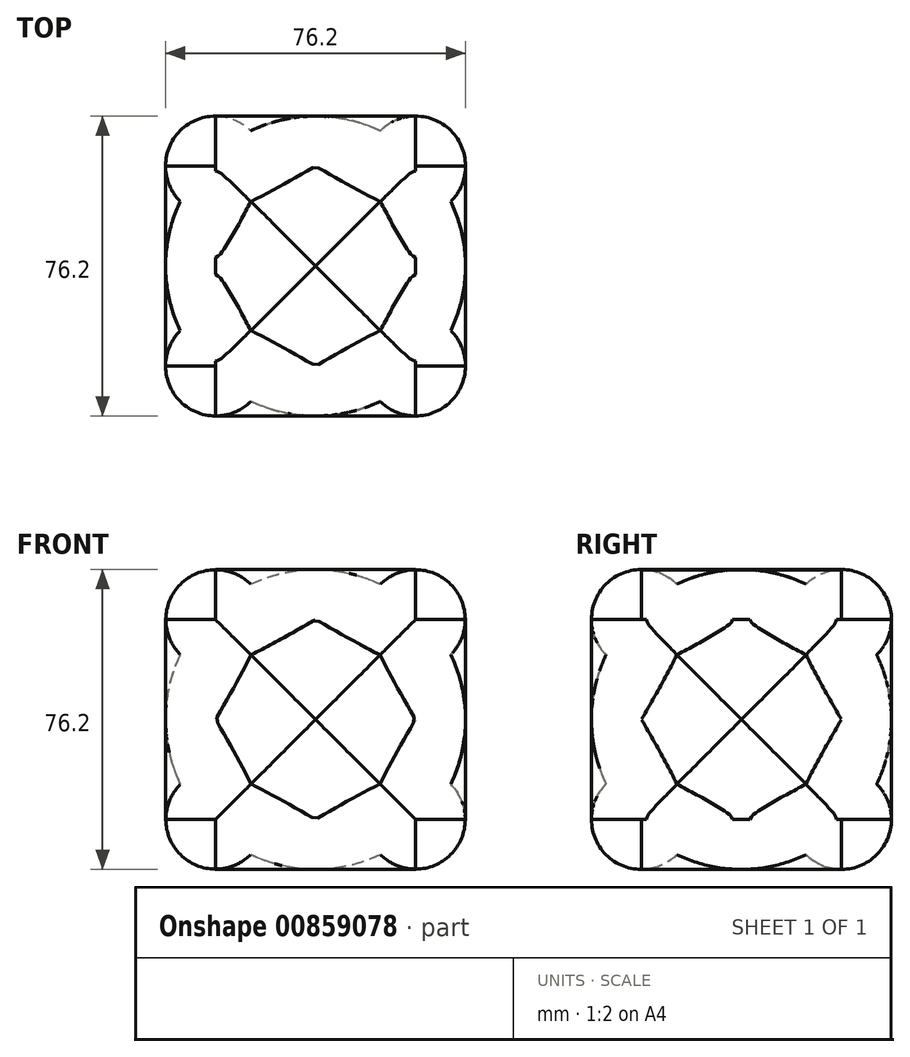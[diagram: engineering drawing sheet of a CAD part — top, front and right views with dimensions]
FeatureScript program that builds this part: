
annotation { "Feature Type Name" : "Feature", "Feature Type Description" : "" }
export const myFeature = defineFeature(function(context is Context, id is Id, definition is map)
    precondition{}
    {
        {
            var Q0;
            Q0=qCreatedBy(makeId("Front.planeOp"),FACE);
            var sketch = newSketch(context, id + "F0", { "sketchPlane" : qUnion([Q0])});
            skCircle(sketch, "E0", {"center": v(0, 0) * mm, "radius": 38.1 * mm});
            skSolve(sketch);
        }
        {
            var Q0;
            Q0 = qSketchRegion(id + "F0", true);
            extrude(context, id + "F1", {"entities" : qUnion([Q0]), "depth" : 25.4 * mm, "offsetDistance" : 25.4 * mm});
        }
        {
            var Q0;
            Q0=qCreatedBy(makeId("Top.planeOp"),FACE);
            var sketch = newSketch(context, id + "F2", { "sketchPlane" : qUnion([Q0])});
            skCircle(sketch, "E1", {"center": v(0, 0) * mm, "radius": 38.1 * mm});
            skSolve(sketch);
        }
        {
            var Q0;
            Q0 = qSketchRegion(id + "F2", true);
            extrude(context, id + "F3", {"entities" : qUnion([Q0]), "operationType" : NewBodyOperationType.ADD, "depth" : 25.4 * mm, "offsetDistance" : 25.4 * mm});
        }
        {
            var Q0;
            Q0=qCreatedBy(makeId("Right.planeOp"),FACE);
            var sketch = newSketch(context, id + "F4", { "sketchPlane" : qUnion([Q0])});
            skCircle(sketch, "E2", {"center": v(0, 0) * mm, "radius": 38.1 * mm});
            skSolve(sketch);
        }
        {
            var Q0;
            Q0 = qSketchRegion(id + "F4", true);
            extrude(context, id + "F5", {"entities" : qUnion([Q0]), "operationType" : NewBodyOperationType.ADD, "depth" : 25.4 * mm, "offsetDistance" : 25.4 * mm});
        }
        {
            var Q0;
            Q0=qCreatedBy(makeId("Top.planeOp"),FACE);
            var sketch = newSketch(context, id + "F6", { "sketchPlane" : qUnion([Q0])});
            skCircle(sketch, "E3", {"center": v(0, 0) * mm, "radius": 38.1 * mm});
            skSolve(sketch);
        }
        {
            var Q0;
            Q0 = qSketchRegion(id + "F6", true);
            extrude(context, id + "F7", {"entities" : qUnion([Q0]), "operationType" : NewBodyOperationType.ADD, "depth" : -25.4 * mm, "offsetDistance" : 25.4 * mm});
        }
        {
            var Q0;
            Q0=qCreatedBy(makeId("Front.planeOp"),FACE);
            var sketch = newSketch(context, id + "F8", { "sketchPlane" : qUnion([Q0])});
            skCircle(sketch, "E4", {"center": v(0, 0) * mm, "radius": 38.1 * mm});
            skSolve(sketch);
        }
        {
            var Q0;
            Q0 = qSketchRegion(id + "F8", true);
            extrude(context, id + "F9", {"entities" : qUnion([Q0]), "operationType" : NewBodyOperationType.ADD, "depth" : -25.4 * mm, "offsetDistance" : 25.4 * mm});
        }
        {
            var Q0;
            Q0=qCreatedBy(makeId("Right.planeOp"),FACE);
            var sketch = newSketch(context, id + "F10", { "sketchPlane" : qUnion([Q0])});
            skCircle(sketch, "E5", {"center": v(0, 0) * mm, "radius": 38.1 * mm});
            skSolve(sketch);
        }
        {
            var Q0;
            Q0 = qSketchRegion(id + "F10", true);
            extrude(context, id + "F11", {"entities" : qUnion([Q0]), "operationType" : NewBodyOperationType.ADD, "depth" : -25.4 * mm, "offsetDistance" : 25.4 * mm});
        }
        {
            var Q0;
            Q0=qCreatedBy(makeId("Front.planeOp"),FACE);
            var sketch = newSketch(context, id + "F12", { "sketchPlane" : qUnion([Q0])});
            skCircle(sketch, "E6", {"center": v(25.4, 25.4) * mm, "radius": 12.64 * mm});
            skCircle(sketch, "E7", {"center": v(-25.4, 25.4) * mm, "radius": 12.64 * mm});
            skCircle(sketch, "E8", {"center": v(25.4, -25.4) * mm, "radius": 12.64 * mm});
            skCircle(sketch, "E9", {"center": v(-25.4, -25.4) * mm, "radius": 12.64 * mm});
            skSolve(sketch);
        }
        {
            var Q0;
            Q0 = qSketchRegion(id + "F12", true);
            extrude(context, id + "F13", {"entities" : qUnion([Q0]), "operationType" : NewBodyOperationType.ADD, "depth" : 25.4 * mm, "offsetDistance" : 25.4 * mm});
        }
        {
            var Q0;
            Q0 = qSketchRegion(id + "F12", true);
            extrude(context, id + "F14", {"entities" : qUnion([Q0]), "operationType" : NewBodyOperationType.ADD, "depth" : -25.4 * mm, "offsetDistance" : 25.4 * mm});
        }
        {
            var Q0;
            Q0=qCreatedBy(makeId("Right.planeOp"),FACE);
            var sketch = newSketch(context, id + "F15", { "sketchPlane" : qUnion([Q0])});
            skCircle(sketch, "E10", {"center": v(-25.4, 25.4) * mm, "radius": 12.7 * mm});
            skCircle(sketch, "E11", {"center": v(25.4, 25.4) * mm, "radius": 12.7 * mm});
            skCircle(sketch, "E12", {"center": v(-25.4, -25.4) * mm, "radius": 12.7 * mm});
            skCircle(sketch, "E13", {"center": v(25.4, -25.4) * mm, "radius": 12.7 * mm});
            skSolve(sketch);
        }
        {
            var Q0;
            Q0 = qSketchRegion(id + "F15", true);
            extrude(context, id + "F16", {"entities" : qUnion([Q0]), "operationType" : NewBodyOperationType.ADD, "depth" : 25.4 * mm, "offsetDistance" : 25.4 * mm});
        }
        {
            var Q0;
            Q0 = qSketchRegion(id + "F15", true);
            extrude(context, id + "F17", {"entities" : qUnion([Q0]), "operationType" : NewBodyOperationType.ADD, "depth" : -25.4 * mm, "offsetDistance" : 25.4 * mm});
        }
        {
            var Q0;
            Q0=qCreatedBy(makeId("Top.planeOp"),FACE);
            var sketch = newSketch(context, id + "F18", { "sketchPlane" : qUnion([Q0])});
            skCircle(sketch, "E14", {"center": v(-25.4, -25.4) * mm, "radius": 12.7 * mm});
            skCircle(sketch, "E15", {"center": v(25.4, -25.4) * mm, "radius": 12.7 * mm});
            skCircle(sketch, "E16", {"center": v(25.4, 25.4) * mm, "radius": 12.7 * mm});
            skCircle(sketch, "E17", {"center": v(-25.4, 25.4) * mm, "radius": 12.7 * mm});
            skSolve(sketch);
        }
        {
            var Q0;
            Q0 = qSketchRegion(id + "F18", true);
            extrude(context, id + "F19", {"entities" : qUnion([Q0]), "operationType" : NewBodyOperationType.ADD, "depth" : 25.4 * mm, "offsetDistance" : 25.4 * mm});
        }
        {
            var Q0;
            Q0 = qSketchRegion(id + "F18", true);
            extrude(context, id + "F20", {"entities" : qUnion([Q0]), "operationType" : NewBodyOperationType.ADD, "depth" : -25.4 * mm, "offsetDistance" : 25.4 * mm});
        }
    });
